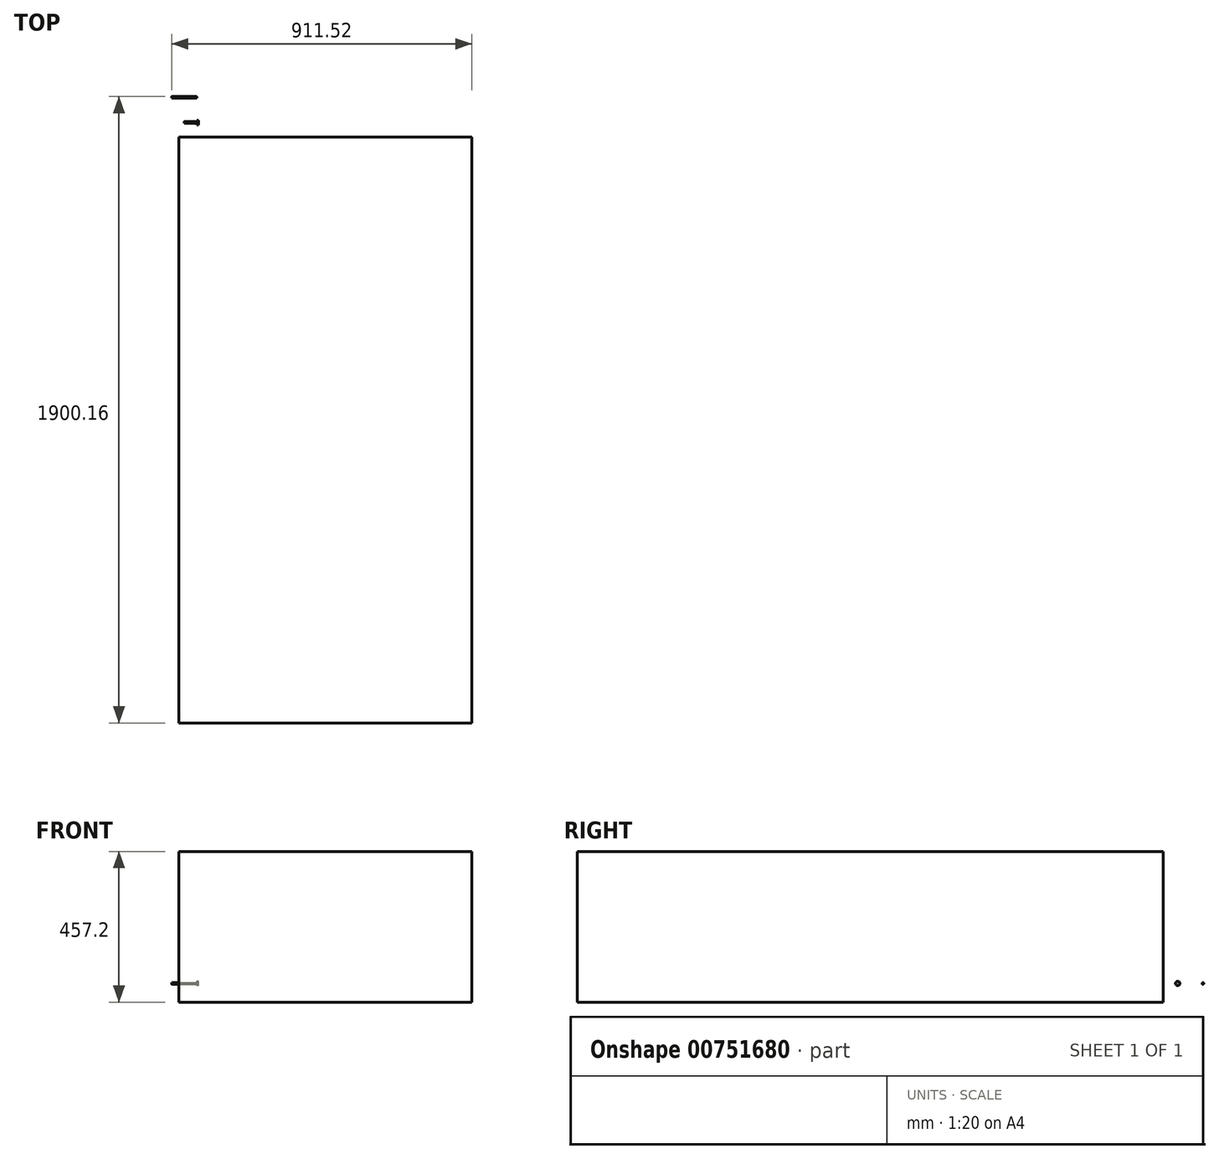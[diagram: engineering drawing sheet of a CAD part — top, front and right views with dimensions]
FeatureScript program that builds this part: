
annotation { "Feature Type Name" : "Feature", "Feature Type Description" : "" }
export const myFeature = defineFeature(function(context is Context, id is Id, definition is map)
    precondition{}
    {
        {
            var Q0;
            Q0=qCreatedBy(makeId("Front.planeOp"),FACE);
            var sketch = newSketch(context, id + "F0", { "sketchPlane" : qUnion([Q0])});
            skLineSegment(sketch, "E0.bottom", {"start": v(-53.68, -13.8) * mm, "end": v(835.32, -13.8) * mm});
            skLineSegment(sketch, "E0.top", {"start": v(-53.68, 443.4) * mm, "end": v(835.32, 443.4) * mm});
            skLineSegment(sketch, "E0.left", {"start": v(-53.68, -13.8) * mm, "end": v(-53.68, 443.4) * mm});
            skLineSegment(sketch, "E0.right", {"start": v(835.32, -13.8) * mm, "end": v(835.32, 443.4) * mm});
            skSolve(sketch);
        }
        {
            var Q0;
            Q0 = qSketchRegion(id + "F0", true);
            extrude(context, id + "F1", {"entities" : qUnion([Q0]), "depth" : 1778 * mm, "offsetDistance" : 25.4 * mm});
        }
        {
            var Q0;
            Q0=qCreatedBy(makeId("Right.planeOp"),FACE);
            var sketch = newSketch(context, id + "F2", { "sketchPlane" : qUnion([Q0])});
            skCircle(sketch, "E1", {"center": v(43.48, 42.8) * mm, "radius": 6.7 * mm});
            skCircle(sketch, "E2", {"center": v(43.48, 42.8) * mm, "radius": 2.48 * mm});
            skSolve(sketch);
        }
        {
            var Q0;
            Q0=makeQuery(id+"F2.imprint","IMPRINT",FACE,{"disambiguationData":[TD([[makeQuery(id+"F2.imprint","IMPRINT",EDGE,{"derivedFrom":sQuery(id+"F2.wireOp",EDGE,"E2")}),1.0]])]});
            extrude(context, id + "F3", {"entities" : qUnion([Q0]), "oppositeDirection" : true, "depth" : 38.1 * mm, "offsetDistance" : 25.4 * mm});
        }
        {
            var Q0;
            Q0=makeQuery(id+"F3.opExtrude","CAP_FACE",FACE,{"disambiguationData":[OSD([sQuery(id+"F2.wireOp",EDGE,"E2")])],"isStart":true});
            var sketch = newSketch(context, id + "F4", { "sketchPlane" : qUnion([Q0])});
            skCircle(sketch, "E3", {"center": v(43.48, 42.8) * mm, "radius": 6.72 * mm});
            skSolve(sketch);
        }
        {
            var Q0;
            Q0 = qSketchRegion(id + "F4", true);
            extrude(context, id + "F5", {"entities" : qUnion([Q0]), "depth" : 4.83 * mm, "offsetDistance" : 25.4 * mm});
        }
        {
            var Q0;
            Q0=makeQuery(id+"F3.opExtrude","SWEPT_BODY",BODY,{"disambiguationData":[OSD([sQuery(id+"F2.wireOp",EDGE,"E2")])]});
            transform(context, id + "F6", {"entities" : qUnion([Q0]), "transformType" : TransformType.TRANSLATION_3D, "dx" : 0 * mm, "dy" : 76.2 * mm, "dz" : 0 * mm, "makeCopy" : true});
        }
        {
            var Q0;
            Q0=makeQuery(id+"F6.opPattern","COPY",FACE,{"derivedFrom":makeQuery(id+"F3.opExtrude","CAP_FACE",FACE,{"disambiguationData":[OSD([sQuery(id+"F2.wireOp",EDGE,"E2")])],"isStart":false}),"instanceName":"1"});
            extrude(context, id + "F7", {"entities" : qUnion([Q0]), "operationType" : NewBodyOperationType.ADD, "depth" : 38.1 * mm, "offsetDistance" : 25.4 * mm});
        }
        {
            var Q0;
            Q0=makeQuery(id+"F1.opExtrude","CAP_FACE",FACE,{"disambiguationData":[OSD([sQuery(id+"F0.wireOp",EDGE,"E0.bottom"),sQuery(id+"F0.wireOp",EDGE,"E0.top"),sQuery(id+"F0.wireOp",EDGE,"E0.left"),sQuery(id+"F0.wireOp",EDGE,"E0.right")])],"isStart":false});
            var sketch = newSketch(context, id + "F8", { "sketchPlane" : qUnion([Q0])});
            skPoint(sketch, "E4", {"position": v(372.64, -13.8) * mm});
            skSolve(sketch);
        }
    });
